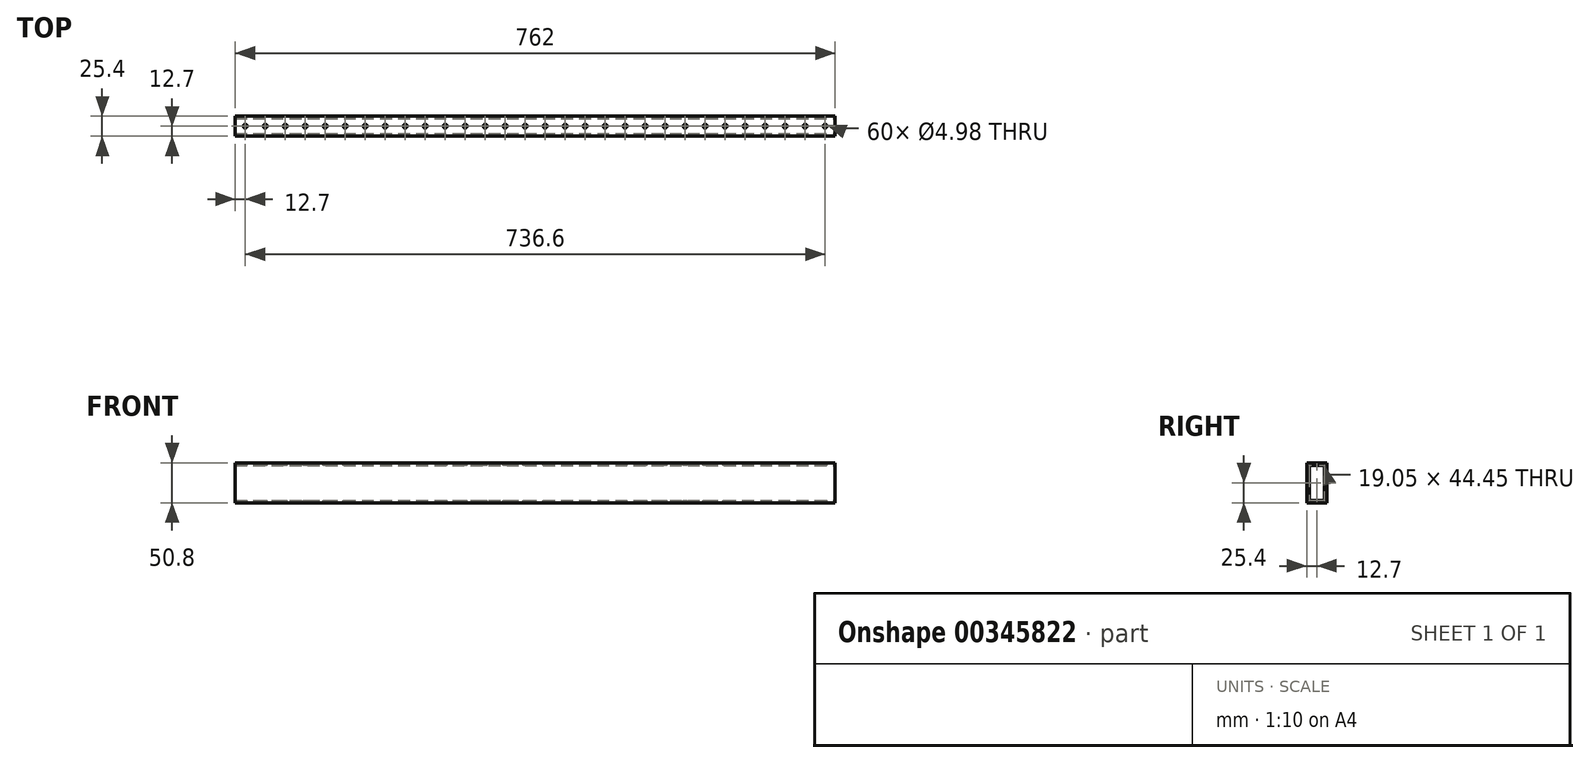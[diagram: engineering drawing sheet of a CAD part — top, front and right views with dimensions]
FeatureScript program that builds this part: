
annotation { "Feature Type Name" : "Feature", "Feature Type Description" : "" }
export const myFeature = defineFeature(function(context is Context, id is Id, definition is map)
    precondition{}
    {
        {
            var Q0;
            Q0=qCreatedBy(makeId("Top.planeOp"),FACE);
            var sketch = newSketch(context, id + "F0", { "sketchPlane" : qUnion([Q0])});
            skLineSegment(sketch, "E0.bottom", {"start": v(-381, 12.7) * mm, "end": v(381, 12.7) * mm});
            skLineSegment(sketch, "E0.top", {"start": v(-381, -12.7) * mm, "end": v(381, -12.7) * mm});
            skLineSegment(sketch, "E0.left", {"start": v(-381, 12.7) * mm, "end": v(-381, -12.7) * mm});
            skLineSegment(sketch, "E0.right", {"start": v(381, 12.7) * mm, "end": v(381, -12.7) * mm});
            skPoint(sketch, "E0.middle", {"position": v(0, 0) * mm});
            skSolve(sketch);
        }
        {
            var Q0;
            Q0 = qSketchRegion(id + "F0", true);
            extrude(context, id + "F1", {"entities" : qUnion([Q0]), "endBound" : BoundingType.SYMMETRIC, "depth" : 50.8 * mm});
        }
        {
            var Q0;
            Q0=makeQuery(id+"F1.opExtrude","SWEPT_FACE",FACE,{"disambiguationData":[OSD([sQuery(id+"F0.wireOp",EDGE,"E0.right")])]});
            var sketch = newSketch(context, id + "F2", { "sketchPlane" : qUnion([Q0])});
            skLineSegment(sketch, "E1.0", {"start": v(-9.52, -22.23) * mm, "end": v(9.53, -22.23) * mm});
            skLineSegment(sketch, "E1.1", {"start": v(-9.52, 22.23) * mm, "end": v(-9.52, -22.22) * mm});
            skLineSegment(sketch, "E1.2", {"start": v(9.53, 22.23) * mm, "end": v(-9.52, 22.23) * mm});
            skLineSegment(sketch, "E1.3", {"start": v(9.53, -22.22) * mm, "end": v(9.53, 22.23) * mm});
            skSolve(sketch);
        }
        {
            var Q0;
            Q0=makeQuery(id+"F2.imprint","IMPRINT",FACE,{"disambiguationData":[TD([[makeQuery(id+"F2.imprint","IMPRINT",EDGE,{"derivedFrom":sQuery(id+"F2.wireOp",EDGE,"E1.0")}),1.0]])]});
            extrude(context, id + "F3", {"entities" : qUnion([Q0]), "operationType" : NewBodyOperationType.REMOVE, "endBound" : BoundingType.THROUGH_ALL, "oppositeDirection" : true, "depth" : 25.4 * mm});
        }
        {
            var Q0;
            Q0=makeQuery(id+"F1.opExtrude","CAP_FACE",FACE,{"disambiguationData":[OSD([sQuery(id+"F0.wireOp",EDGE,"E0.bottom"),sQuery(id+"F0.wireOp",EDGE,"E0.top"),sQuery(id+"F0.wireOp",EDGE,"E0.left"),sQuery(id+"F0.wireOp",EDGE,"E0.right")])],"isStart":false});
            var sketch = newSketch(context, id + "F4", { "sketchPlane" : qUnion([Q0])});
            skLineSegment(sketch, "E2", {"start": v(-381, 0) * mm, "end": v(381, 0) * mm, "construction": true});
            skCircle(sketch, "E3", {"center": v(-368.3, 0) * mm, "radius": 2.49 * mm});
            skCircle(sketch, "E4.1.0.0", {"center": v(-342.9, 0) * mm, "radius": 2.49 * mm});
            skCircle(sketch, "E4.2.0.0", {"center": v(-317.5, 0) * mm, "radius": 2.49 * mm});
            skCircle(sketch, "E4.3.0.0", {"center": v(-292.1, 0) * mm, "radius": 2.49 * mm});
            skCircle(sketch, "E4.4.0.0", {"center": v(-266.7, 0) * mm, "radius": 2.49 * mm});
            skCircle(sketch, "E4.5.0.0", {"center": v(-241.3, 0) * mm, "radius": 2.49 * mm});
            skCircle(sketch, "E4.6.0.0", {"center": v(-215.9, 0) * mm, "radius": 2.49 * mm});
            skCircle(sketch, "E4.7.0.0", {"center": v(-190.5, 0) * mm, "radius": 2.49 * mm});
            skCircle(sketch, "E4.8.0.0", {"center": v(-165.1, 0) * mm, "radius": 2.49 * mm});
            skCircle(sketch, "E4.9.0.0", {"center": v(-139.7, 0) * mm, "radius": 2.49 * mm});
            skCircle(sketch, "E4.10.0.0", {"center": v(-114.3, 0) * mm, "radius": 2.49 * mm});
            skCircle(sketch, "E4.11.0.0", {"center": v(-88.9, 0) * mm, "radius": 2.49 * mm});
            skCircle(sketch, "E4.12.0.0", {"center": v(-63.5, 0) * mm, "radius": 2.49 * mm});
            skCircle(sketch, "E4.13.0.0", {"center": v(-38.1, 0) * mm, "radius": 2.49 * mm});
            skCircle(sketch, "E4.14.0.0", {"center": v(-12.7, 0) * mm, "radius": 2.49 * mm});
            skCircle(sketch, "E4.15.0.0", {"center": v(12.7, 0) * mm, "radius": 2.49 * mm});
            skCircle(sketch, "E4.16.0.0", {"center": v(38.1, 0) * mm, "radius": 2.49 * mm});
            skCircle(sketch, "E4.17.0.0", {"center": v(63.5, 0) * mm, "radius": 2.49 * mm});
            skCircle(sketch, "E4.18.0.0", {"center": v(88.9, 0) * mm, "radius": 2.49 * mm});
            skCircle(sketch, "E4.19.0.0", {"center": v(114.3, 0) * mm, "radius": 2.49 * mm});
            skCircle(sketch, "E4.20.0.0", {"center": v(139.7, 0) * mm, "radius": 2.49 * mm});
            skCircle(sketch, "E4.21.0.0", {"center": v(165.1, 0) * mm, "radius": 2.49 * mm});
            skCircle(sketch, "E4.22.0.0", {"center": v(190.5, 0) * mm, "radius": 2.49 * mm});
            skCircle(sketch, "E4.23.0.0", {"center": v(215.9, 0) * mm, "radius": 2.49 * mm});
            skCircle(sketch, "E4.24.0.0", {"center": v(241.3, 0) * mm, "radius": 2.49 * mm});
            skCircle(sketch, "E4.25.0.0", {"center": v(266.7, 0) * mm, "radius": 2.49 * mm});
            skCircle(sketch, "E4.26.0.0", {"center": v(292.1, 0) * mm, "radius": 2.49 * mm});
            skCircle(sketch, "E4.27.0.0", {"center": v(317.5, 0) * mm, "radius": 2.49 * mm});
            skCircle(sketch, "E4.28.0.0", {"center": v(342.9, 0) * mm, "radius": 2.49 * mm});
            skCircle(sketch, "E4.29.0.0", {"center": v(368.3, 0) * mm, "radius": 2.49 * mm});
            skLineSegment(sketch, "E4.direction1", {"start": v(-368.3, 0) * mm, "end": v(-342.9, 0) * mm, "construction": true});
            skSolve(sketch);
        }
        {
            var Q0;
            Q0 = qSketchRegion(id + "F4", true);
            extrude(context, id + "F5", {"entities" : qUnion([Q0]), "operationType" : NewBodyOperationType.REMOVE, "endBound" : BoundingType.THROUGH_ALL, "oppositeDirection" : true, "depth" : 25.4 * mm});
        }
    });
